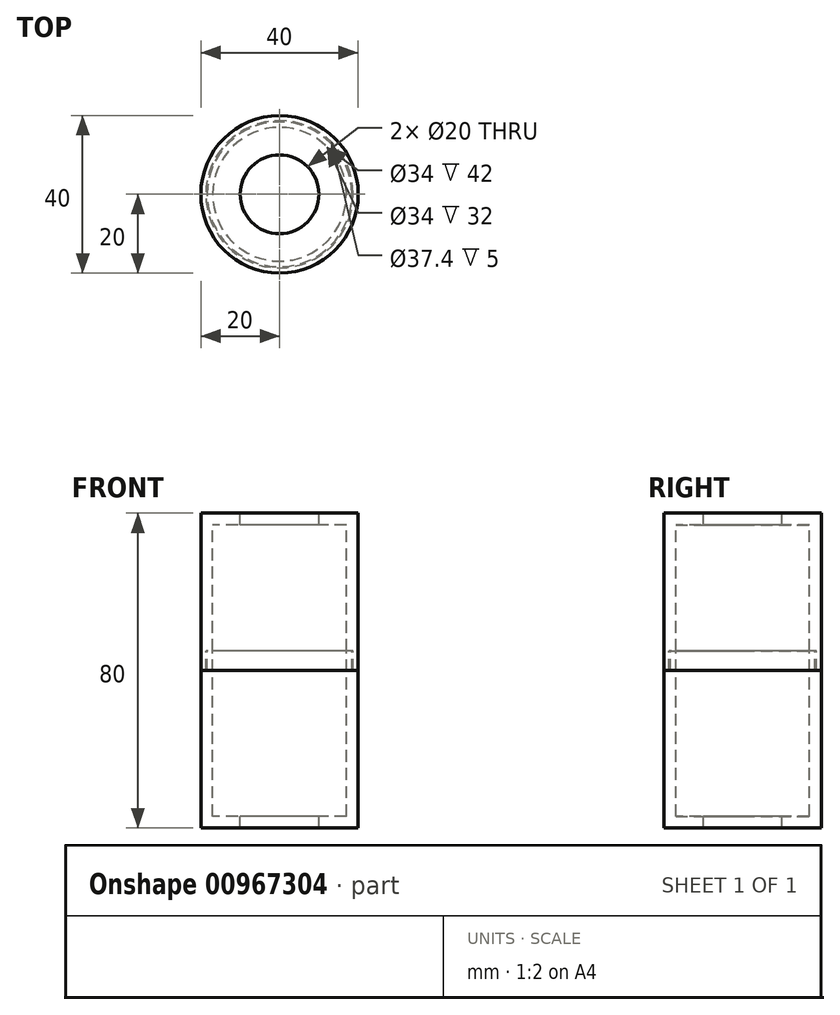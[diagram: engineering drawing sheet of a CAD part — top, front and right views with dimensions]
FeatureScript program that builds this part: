
annotation { "Feature Type Name" : "Feature", "Feature Type Description" : "" }
export const myFeature = defineFeature(function(context is Context, id is Id, definition is map)
    precondition{}
    {
        {
            var Q0;
            Q0=qCreatedBy(makeId("Front.planeOp"),FACE);
            var sketch = newSketch(context, id + "F0", { "sketchPlane" : qUnion([Q0])});
            skLineSegment(sketch, "E0", {"start": v(0, 0) * mm, "end": v(0, 32.37) * mm, "construction": true});
            skLineSegment(sketch, "E1", {"start": v(10, 40) * mm, "end": v(20, 40) * mm});
            skLineSegment(sketch, "E2", {"start": v(20, 40) * mm, "end": v(20, 0) * mm});
            skLineSegment(sketch, "E3.0", {"start": v(17, 37) * mm, "end": v(17, 5) * mm});
            skLineSegment(sketch, "E3.1", {"start": v(10, 37) * mm, "end": v(17, 37) * mm});
            skLineSegment(sketch, "E4", {"start": v(10, 37) * mm, "end": v(10, 40) * mm});
            skPoint(sketch, "E5.orphan", {"position": v(0, 40) * mm});
            skLineSegment(sketch, "E6", {"start": v(20, 0) * mm, "end": v(18.7, 0) * mm});
            skLineSegment(sketch, "E7", {"start": v(18.7, 0) * mm, "end": v(18.7, 5) * mm});
            skLineSegment(sketch, "E8", {"start": v(18.7, 5) * mm, "end": v(17, 5) * mm});
            skPoint(sketch, "E9.orphan", {"position": v(17, 0) * mm});
            skSolve(sketch);
        }
        {
            var Q0;
            Q0=makeQuery(id+"F0.imprint","IMPRINT",FACE,{"disambiguationData":[TD([[makeQuery(id+"F0.imprint","IMPRINT",EDGE,{"derivedFrom":sQuery(id+"F0.wireOp",EDGE,"E1")}),-1.0]])]});
            var Q1;
            Q1=sQuery(id+"F0.wireOp",EDGE,"E0");
            revolve(context, id + "F1", {"surfaceOperationType" : NewSurfaceOperationType.NEW, "entities" : qUnion([Q0]), "axis" : qUnion([Q1]), "revolveType" : RevolveType.FULL, "oppositeDirection" : true});
        }
        {
            var Q0;
            Q0=qCreatedBy(makeId("Front.planeOp"),FACE);
            var sketch = newSketch(context, id + "F2", { "sketchPlane" : qUnion([Q0])});
            skLineSegment(sketch, "E10", {"start": v(0, 0) * mm, "end": v(0, -16) * mm, "construction": true});
            skLineSegment(sketch, "E11", {"start": v(20, 0) * mm, "end": v(20, -40) * mm});
            skLineSegment(sketch, "E12", {"start": v(20, -40) * mm, "end": v(10, -40) * mm});
            skLineSegment(sketch, "E13.0", {"start": v(17, -37) * mm, "end": v(10, -37) * mm});
            skLineSegment(sketch, "E13.1", {"start": v(17, 0) * mm, "end": v(17, -37) * mm});
            skLineSegment(sketch, "E14", {"start": v(10, -37) * mm, "end": v(10, -40) * mm});
            skPoint(sketch, "E15.orphan", {"position": v(0, -40) * mm});
            skLineSegment(sketch, "E16", {"start": v(17, 0) * mm, "end": v(17, 5) * mm});
            skLineSegment(sketch, "E17", {"start": v(17, 5) * mm, "end": v(18.4, 5) * mm});
            skLineSegment(sketch, "E18", {"start": v(18.4, 5) * mm, "end": v(18.4, 0) * mm});
            skLineSegment(sketch, "E19", {"start": v(18.4, 0) * mm, "end": v(20, 0) * mm});
            skSolve(sketch);
        }
        {
            var Q0;
            Q0=makeQuery(id+"F2.imprint","IMPRINT",FACE,{"disambiguationData":[TD([[makeQuery(id+"F2.imprint","IMPRINT",EDGE,{"derivedFrom":sQuery(id+"F2.wireOp",EDGE,"E11")}),-1.0]])]});
            var Q1;
            Q1=sQuery(id+"F2.wireOp",EDGE,"E10");
            revolve(context, id + "F3", {"surfaceOperationType" : NewSurfaceOperationType.NEW, "entities" : qUnion([Q0]), "axis" : qUnion([Q1]), "revolveType" : RevolveType.FULL});
        }
    });
